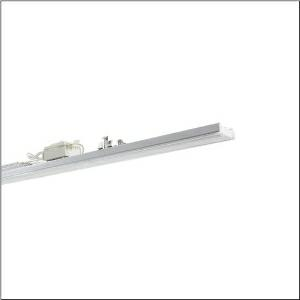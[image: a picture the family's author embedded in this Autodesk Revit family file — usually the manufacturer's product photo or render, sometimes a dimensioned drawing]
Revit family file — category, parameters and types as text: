
# Revit family: licross_r__11_recessed_mo_51tl11dv4fxg_29b5
name_source: partatom
category: Lighting Fixtures
units: mm (PartAtom-declared; Revit-internal decimal feet)

## family parameters
Cut with Voids When Loaded = No
Host = Face
Light Source = No
Part Type = Normal
Room Calculation Point = No
Round Connector Dimension = Use Diameter
Shared = No

## types (1)
- --- (1 x LED, 15120 lm, 84.1 W, 4000K)
    Apparent Load = 84 VA
    CIE Flux Codes = 89 96 99 100 100
    Color Rendering = 80
    Color Temperature = 4000K
    Default Elevation = 1800 mm
    Description = Licross® 11 Recessed MO, luminaire insert, of sheet steel, coil coated, white, length: 2.250mm, width: 66mm, height: 67mm, LED rated luminous flux: 15.120lm, light colour: 840, control gear: DALI 2, with plug, 5-pole, with phase selection, mains connection: 220..240V, AC, 50/60Hz, rated input power: 84W, halogen-free wiring, primary light control with lens, of plastic, primary optical cover: cover, of PMMA, light emission: direct distribution, primary light characteristic: symmetric, protection rating (complete): IP40, insulation class (complete): insulation class I (protective earthing), certification: CE, ENEC, VDE, UKCA, protection symbol: D if used in an environment without relevant dust loads with corresponding accessories, impact resistance: IK06, permissible ambient temperature for indoor applications: -25..+35°C, corresponds to IFS (International Featured Standards) requirements for safety and quality in the food industry, reducing of maximum allowable ambient temperature of 5°C with ceiling mounting, LABS conformity tested according to VDMA 24364:2018-05, packaging unit: 1 piece
    Height = 58 mm
    Lamp = 1 x LED
    Lamp Light Flux = 15120 lm
    Lamp Power = 84.1 W
    Lamp count = 1
    Length = 2250 mm
    Luminous efficacy = 180 lm/W
    Manufacturer = Siteco
    ModVariant = No
    Model = 51TL11DV4FXG
    Mounting Place = Ceiling
    Mounting Type = Pendant
    Number of Poles = 1
    OnlyDefault = Yes
    Power Factor = 1
    Product Name = Licross® 11 Recessed MO
    Product group = luminaire insert
    ProductGroupID = 902
    Protection Class = Protection class I
    Protection Degree = IP 40
    RLX_Detail_Level = 1
    RLX_Emergency_Light_Flux = 0 lm
    RLX_Emergency_Type = 0
    RLX_Emergency_Type_DB = No
    RlxData = <blob elided: 29353 chars, md5=74830877>
    Socket = socket
    Standby Power = 0 W
    System Light Flux = 15120 lm
    System Power = 84 W
    Type Comments = factory setting: luminous flux: 100 % | dim-lin: 254 | 378 mA
    Type Image = l_1296930.jpg
    URL = http://relux.com
    VarID = @adj_098656
    Voltage = 0 V
    Weight = 0.00 kg
    Width = 66 mm

## geometry (parser evidence)
native form markers: Blend x4, Sweep x9
no freeform markers — native parametric forms only
